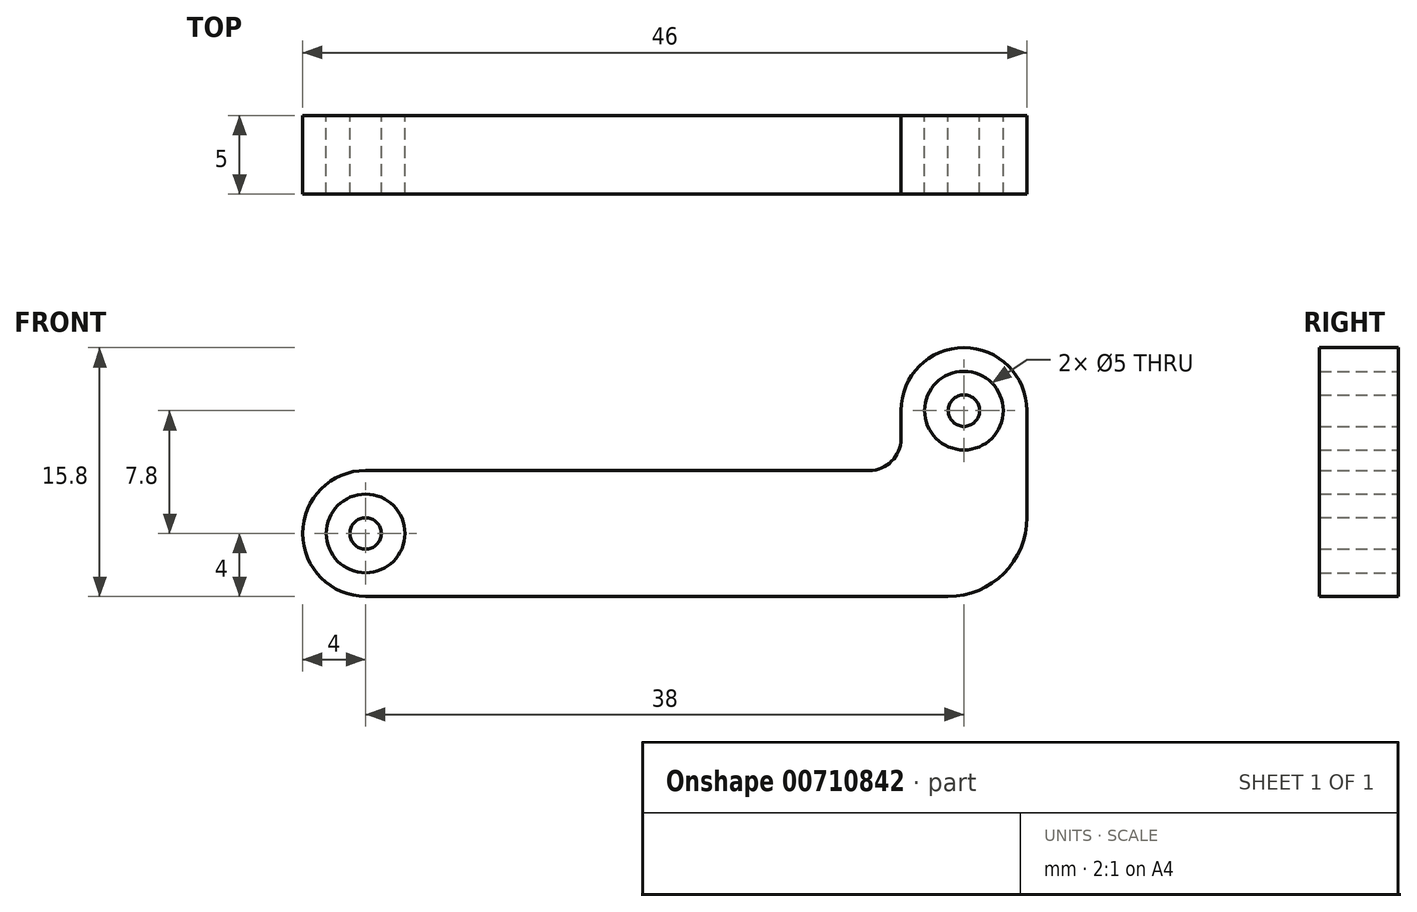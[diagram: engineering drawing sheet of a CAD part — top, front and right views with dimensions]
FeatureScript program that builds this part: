
annotation { "Feature Type Name" : "Feature", "Feature Type Description" : "" }
export const myFeature = defineFeature(function(context is Context, id is Id, definition is map)
    precondition{}
    {
        {
            var Q0;
            Q0=qCreatedBy(makeId("Front.planeOp"),FACE);
            var sketch = newSketch(context, id + "F0", { "sketchPlane" : qUnion([Q0])});
            skCircle(sketch, "E0", {"center": v(0, 0) * mm, "radius": 2.5 * mm});
            skCircle(sketch, "E1", {"center": v(0, 0) * mm, "radius": 1 * mm});
            skArc(sketch, "E2", {"start": v(0, 4) * mm, "mid": v(-4, 0) * mm, "end": v(0, -4) * mm});
            skCircle(sketch, "E3", {"center": v(38, 7.8) * mm, "radius": 1 * mm});
            skCircle(sketch, "E4", {"center": v(38, 7.8) * mm, "radius": 2.5 * mm});
            skArc(sketch, "E5", {"start": v(42, 7.8) * mm, "mid": v(38, 11.8) * mm, "end": v(34, 7.8) * mm});
            skLineSegment(sketch, "E6", {"start": v(0, 4) * mm, "end": v(32, 4) * mm});
            skLineSegment(sketch, "E7", {"start": v(34, 7.8) * mm, "end": v(34, 6) * mm});
            skLineSegment(sketch, "E8", {"start": v(0, -4) * mm, "end": v(37, -4) * mm});
            skLineSegment(sketch, "E9", {"start": v(42, 7.8) * mm, "end": v(42, 1) * mm});
            skPoint(sketch, "E10.visualSharp", {"position": v(34, 4) * mm});
            skArc(sketch, "E10.filletArc", {"start": v(32, 4) * mm, "mid": v(33.41, 4.59) * mm, "end": v(34, 6) * mm});
            skPoint(sketch, "E11.visualSharp", {"position": v(42, -4) * mm});
            skArc(sketch, "E11.filletArc", {"start": v(37, -4) * mm, "mid": v(40.54, -2.54) * mm, "end": v(42, 1) * mm});
            skSolve(sketch);
        }
        {
            var Q0;
            Q0=makeQuery(id+"F0.imprint","IMPRINT",FACE,{"disambiguationData":[TD([[makeQuery(id+"F0.imprint","IMPRINT",EDGE,{"derivedFrom":sQuery(id+"F0.wireOp",EDGE,"E0")}),-1.0]])]});
            var Q1;
            Q1=makeQuery(id+"F0.imprint","IMPRINT",FACE,{"disambiguationData":[TD([[makeQuery(id+"F0.imprint","IMPRINT",EDGE,{"derivedFrom":sQuery(id+"F0.wireOp",EDGE,"E1")}),1.0]])]});
            var Q2;
            Q2=makeQuery(id+"F0.imprint","IMPRINT",FACE,{"disambiguationData":[TD([[makeQuery(id+"F0.imprint","IMPRINT",EDGE,{"derivedFrom":sQuery(id+"F0.wireOp",EDGE,"E3")}),1.0]])]});
            extrude(context, id + "F1", {"entities" : qUnion([Q0, Q1, Q2]), "depth" : 5 * mm, "offsetDistance" : 25 * mm});
        }
    });
